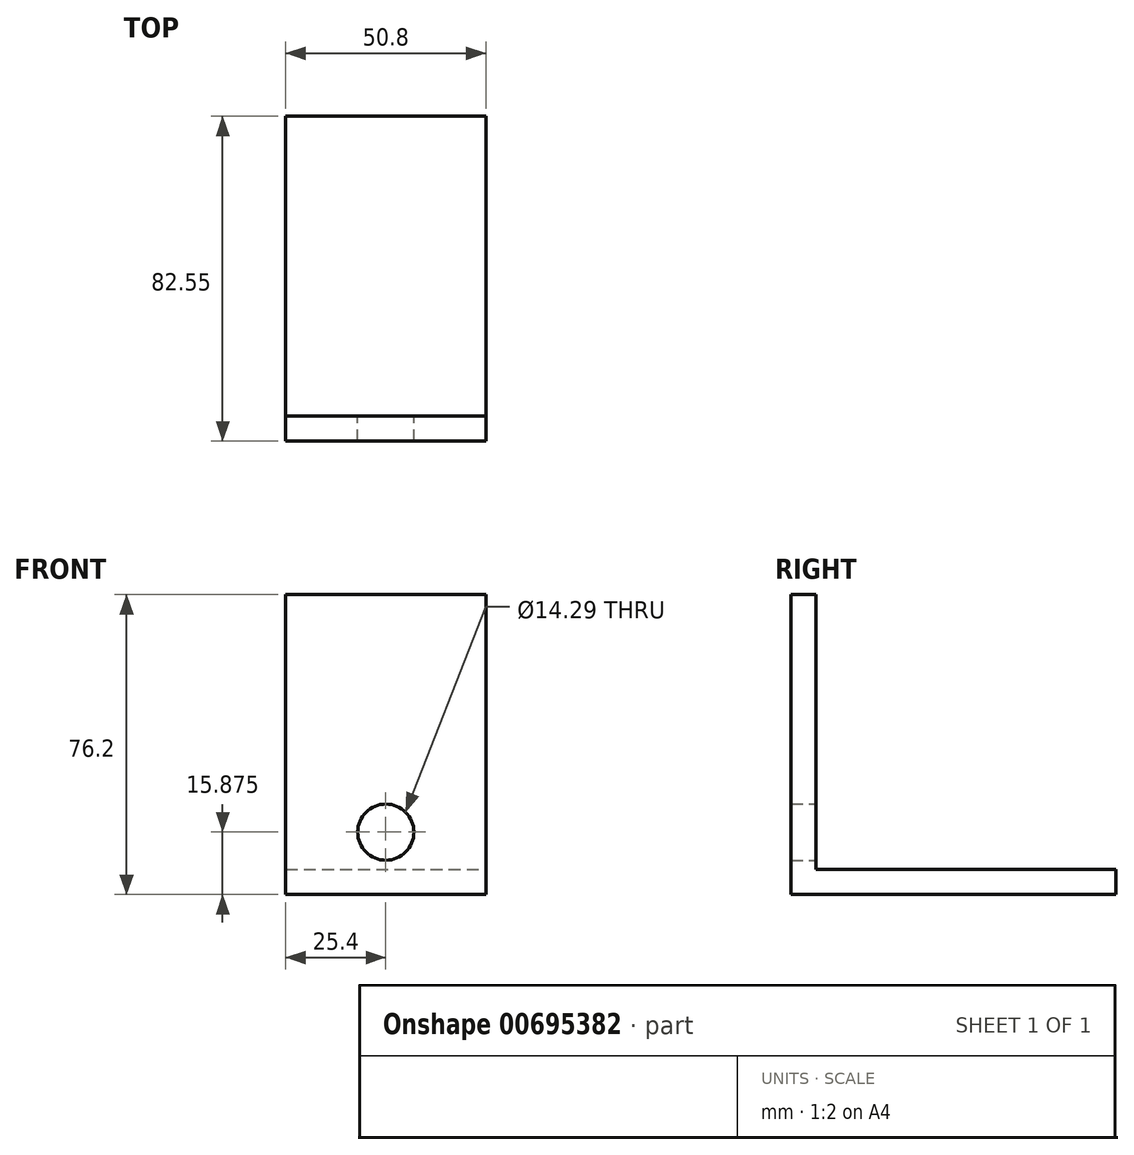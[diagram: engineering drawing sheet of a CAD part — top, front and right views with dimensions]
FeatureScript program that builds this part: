
annotation { "Feature Type Name" : "Feature", "Feature Type Description" : "" }
export const myFeature = defineFeature(function(context is Context, id is Id, definition is map)
    precondition{}
    {
        {
            var Q0;
            Q0=qCreatedBy(makeId("Front.planeOp"),FACE);
            var sketch = newSketch(context, id + "F0", { "sketchPlane" : qUnion([Q0])});
            skLineSegment(sketch, "E0.bottom", {"start": v(25.4, -38.1) * mm, "end": v(-25.4, -38.1) * mm});
            skLineSegment(sketch, "E0.top", {"start": v(25.4, 38.1) * mm, "end": v(-25.4, 38.1) * mm});
            skLineSegment(sketch, "E0.left", {"start": v(25.4, -38.1) * mm, "end": v(25.4, 38.1) * mm});
            skLineSegment(sketch, "E0.right", {"start": v(-25.4, -38.1) * mm, "end": v(-25.4, 38.1) * mm});
            skPoint(sketch, "E0.middle", {"position": v(0, 0) * mm});
            skCircle(sketch, "E1", {"center": v(0, -22.23) * mm, "radius": 7.14 * mm});
            skSolve(sketch);
        }
        {
            var Q0;
            Q0 = qSketchRegion(id + "F0", true);
            extrude(context, id + "F1", {"entities" : qUnion([Q0]), "depth" : 6.35 * mm, "offsetDistance" : 25.4 * mm});
        }
        {
            var Q0;
            Q0=makeQuery(id+"F1.opExtrude","SWEPT_FACE",FACE,{"disambiguationData":[OSD([sQuery(id+"F0.wireOp",EDGE,"E0.left")])]});
            var sketch = newSketch(context, id + "F2", { "sketchPlane" : qUnion([Q0])});
            skLineSegment(sketch, "E2.bottom", {"start": v(0, -38.1) * mm, "end": v(76.2, -38.1) * mm});
            skLineSegment(sketch, "E2.top", {"start": v(0, -31.75) * mm, "end": v(76.2, -31.75) * mm});
            skLineSegment(sketch, "E2.left", {"start": v(0, -38.1) * mm, "end": v(0, -31.75) * mm});
            skLineSegment(sketch, "E2.right", {"start": v(76.2, -38.1) * mm, "end": v(76.2, -31.75) * mm});
            skSolve(sketch);
        }
        {
            var Q0;
            Q0=makeQuery(id+"F2.imprint","IMPRINT",FACE,{"disambiguationData":[TD([[makeQuery(id+"F2.imprint","IMPRINT",EDGE,{"derivedFrom":sQuery(id+"F2.wireOp",EDGE,"E2.bottom")}),1.0]])]});
            extrude(context, id + "F3", {"entities" : qUnion([Q0]), "operationType" : NewBodyOperationType.ADD, "oppositeDirection" : true, "depth" : 50.8 * mm, "offsetDistance" : 25.4 * mm});
        }
    });
